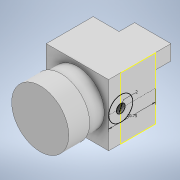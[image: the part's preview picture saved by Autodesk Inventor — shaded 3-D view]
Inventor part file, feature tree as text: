
AUTODESK INVENTOR PART (.ipt)
format: ipt  version: 2020 (Build 240168000, 168)  size: 204,800 bytes
history: native  units: mm
features: extrude x12, sketch x8, projected_geometry x6, plane x1, fillet x1
ambient origin geometry x8: Origin, YZ Plane, XZ Plane, XY Plane, X Axis, Y Axis, Z Axis, Center Point
bodies: Solid1 (feature_tree)
feature tree (28):
  extrude  "Extrusion1"  Depth=14.3mm
  sketch  "Sketch2"  dims[d2=8.0mm d3=0.0mm d4=10.75mm]
  extrude  "Extrusion2"  Depth=10.75mm
  extrude  "Extrusion3"  Depth=8.0mm TaperAngle=0.0deg
  plane  "Work Plane1"
  sketch  "Sketch3"  dims[d5=2.0mm d6=8.0mm d7=0.0mm]
  extrude  "Extrusion4"  Depth=12.3mm
  extrude  "Extrusion5"  Depth=8.0mm TaperAngle=0.0deg
  extrude  "Extrusion6"  Depth=14.5mm
  extrude  "Extrusion7"  Depth=13.1mm
  extrude  "Extrusion8"  Depth=19.3mm
  extrude  "Extrusion9"  TaperAngle=0.0deg  [1 undecoded]
  fillet  "Fillet1"  Radius=5.0mm
  extrude  "Extrusion10"  Depth=8.35mm
  extrude  "Extrusion11"  Depth=3.45mm
  extrude  "Extrusion12"  Depth=3.55mm TaperAngle=0.0deg
  sketch  "Sketch1"  dims[d0=14.15mm d1=14.3mm]
  projected_geometry  "Projected Loop1"
  projected_geometry  "Projected Loop2"
  projected_geometry  "Projected Loop3"
  projected_geometry  "Projected Loop4"
  sketch  "Sketch4"  dims[d8=8.0mm d9=0.0mm d10=12.3mm]
  sketch  "Sketch5"  dims[d11=8.0mm d12=0.0mm d13=8.0mm d14=0.0mm]
  sketch  "Sketch6"  dims[d15=8.0mm d16=0.0mm d17=14.5mm]
  projected_geometry  "Projected Loop5"
  sketch  "Sketch7"  dims[d18=0.0mm d19=0.0mm d20=13.1mm]
  projected_geometry  "Projected Loop6"
  sketch  "Sketch8"  dims[d21=8.0mm d22=0.0mm d23=19.3mm d24=0.0mm d25=0.0mm d26=5.0mm d28=8.35mm d29=3.45mm d30=3.55mm d31=0.0mm d32=3.55mm d33=0.0mm d34=3.55mm d35=0.0mm]
note: 1 required parameter value undecoded (feature->parameter linkage not recoverable at this tier; creation-order binding heuristic only, values carry confidence <= 0.55)
